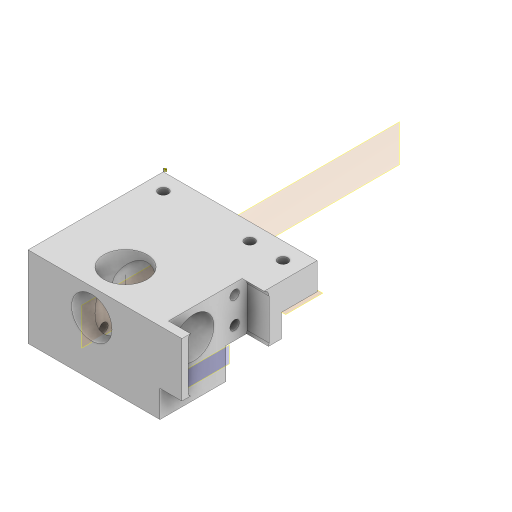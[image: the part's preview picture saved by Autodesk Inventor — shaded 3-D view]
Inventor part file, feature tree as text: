
AUTODESK INVENTOR PART (.ipt)
format: ipt  version: 2024.1 (Build 281209000, 209)  size: 401,920 bytes
history: native  units: mm
features: reference x15, extrude x13, sketch x11, plane x10, projected_geometry x7, other x5
ambient origin geometry x8: Origin, YZ Plane, XZ Plane, XY Plane, X Axis, Y Axis, Z Axis, Center Point
bodies: Body1 (feature_tree)
feature tree (61):
  plane  "Arbeitsebene6"
  extrude  "Extrusion12"  Depth=0.5mm
  extrude  "Extrusion13"  Depth=12.0mm
  plane  "Arbeitsebene7"
  plane  "Arbeitsebene8"
  plane  "Arbeitsebene9"
  plane  "Arbeitsebene10"
  sketch  "Skizze21"  dims[d76=35.97mm d77=0.0mm d87=0.5mm]
  plane  "Arbeitsebene11"
  extrude  "Extrusion18"  Depth=0.5mm
  plane  "Arbeitsebene12"
  extrude  "Extrusion22"  TaperAngle=0.0deg  [1 undecoded]
  extrude  "Extrusion23"  Depth=0.5mm
  extrude  "Extrusion27"  TaperAngle=0.0deg  [1 undecoded]
  sketch  "Skizze31"  dims[d107=12.0mm d108=0.0mm d109=0.0mm d110=0.0mm]
  plane  "Arbeitsebene13"
  extrude  "Extrusion28"  Depth=10.0mm
  extrude  "Extrusion29"  Depth=10.0mm TaperAngle=0.0deg
  sketch  "Skizze33"  dims[d111=10.0mm d112=0.0mm d113=0.1mm]
  plane  "Arbeitsebene14"
  extrude  "Extrusion30"  Depth=6.0mm
  sketch  "Skizze35"  dims[d114=0.1mm d116=10.0mm d117=0.0mm]
  plane  "Arbeitsebene15"
  extrude  "Extrusion32"  Depth=2.0mm
  extrude  "Extrusion33"  Depth=10.0mm
  extrude  "Extrusion34"  Depth=10.0mm
  extrude  "Extrusion35"  Depth=10.0mm TaperAngle=0.0deg
  sketch  "Skizze13"  dims[d58=8.0mm d59=0.0mm d60=0.5mm]
  reference  "Referenz11"
  reference  "Referenz12"
  reference  "Referenz13"
  reference  "Referenz14"
  sketch  "Skizze16"  dims[d62=8.0mm d63=0.0mm d75=12.0mm]
  projected_geometry  "Projizierte Kontur9"
  reference  "Referenz15"
  reference  "Referenz25"
  reference  "Referenz26"
  reference  "Referenz27"
  sketch  "Skizze26"  dims[d88=10.0mm d89=0.0mm d90=0.0mm d91=0.0mm]
  sketch  "Skizze30"  dims[d93=20.0mm d94=0.5mm]
  reference  "Referenz30"
  reference  "Referenz31"
  reference  "Referenz32"
  reference  "Referenz33"
  reference  "Referenz34"
  reference  "Referenz35"
  reference  "Referenz36"
  projected_geometry  "Projizierte Kontur16"
  projected_geometry  "Projizierte Kontur17"
  sketch  "Skizze36"  dims[d120=6.0mm d121=9.5mm]
  projected_geometry  "Projizierte Kontur18"
  sketch  "Skizze37"  dims[d122=9.5mm d123=2.0mm]
  projected_geometry  "Projizierte Kontur19"
  projected_geometry  "Projizierte Kontur20"
  sketch  "Skizze38"  dims[d124=2.0mm d125=2.0mm d126=2.5mm d127=10.0mm d128=0.0mm d129=12.0mm d130=8.0mm d131=0.0mm d132=12.8mm d133=0.0mm d134=0.0mm d135=2.8mm d136=8.0mm d137=0.0mm d15=0.5mm d16=0.872665mm d17=0.5mm d18=0.872665mm]
  projected_geometry  "Projizierte Kontur21"
  other  "Assemlby_lightsheet_generator_passive_v2.iam"
  other  "30_Scanlens_Laseradaper_lid_v1:1"
  other  "00_SMAConnector_fiber copy:1"
  other  "30_Lightsheet_generator_passive_lid_v1:1"
  other  "30_Laser_to_M12Adapter:1"
note: 2 required parameter values undecoded (feature->parameter linkage not recoverable at this tier; creation-order binding heuristic only, values carry confidence <= 0.55)
